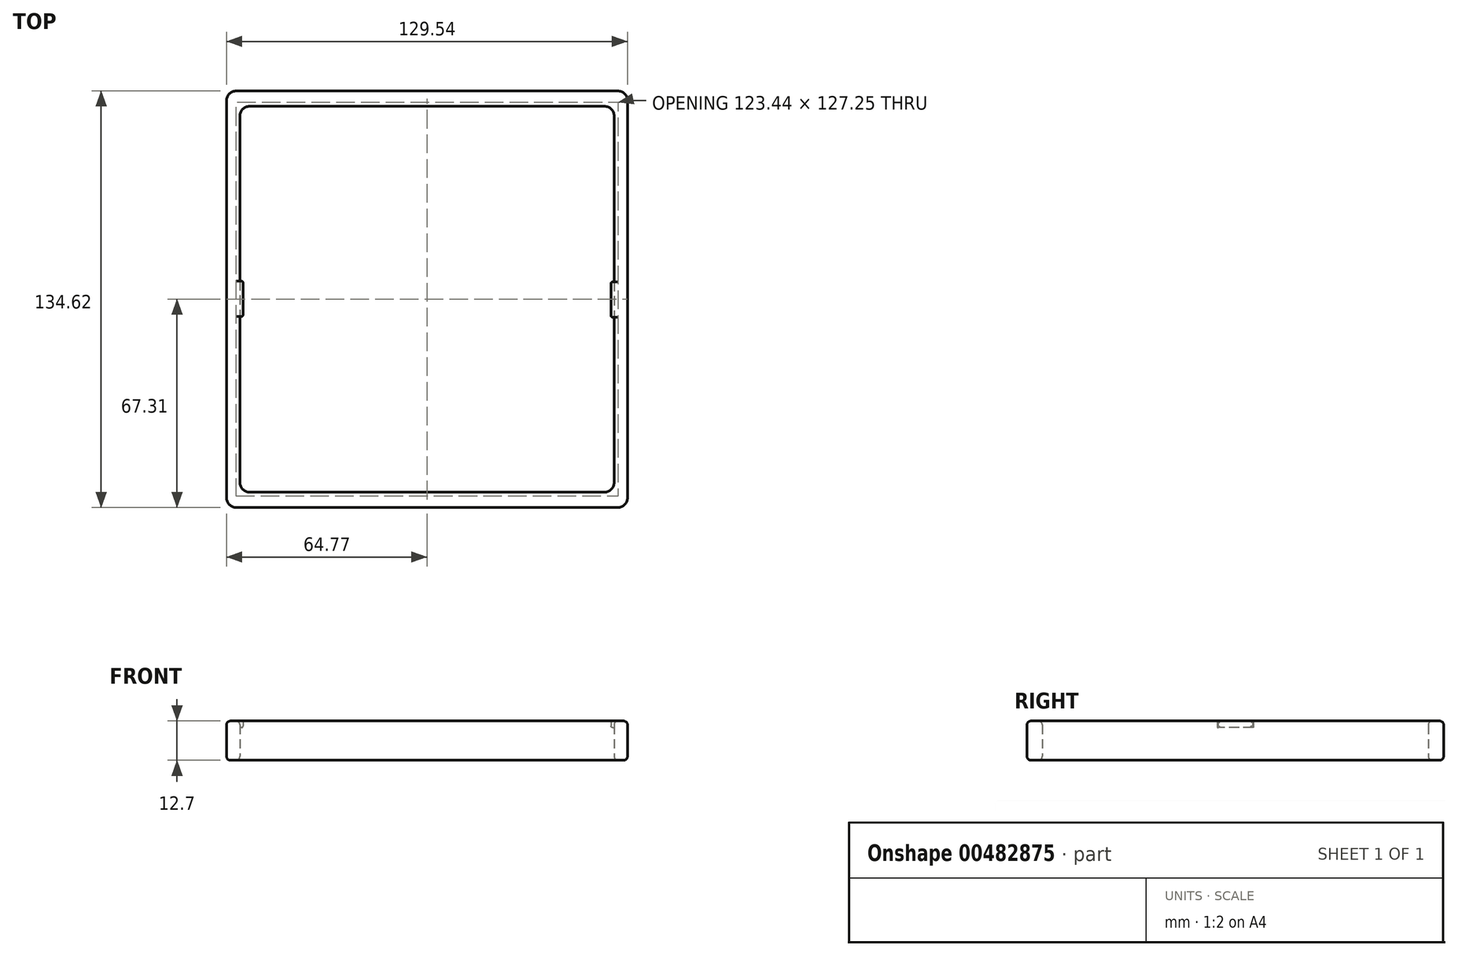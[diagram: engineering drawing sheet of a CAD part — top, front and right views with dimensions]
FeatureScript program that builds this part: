
annotation { "Feature Type Name" : "Feature", "Feature Type Description" : "" }
export const myFeature = defineFeature(function(context is Context, id is Id, definition is map)
    precondition{}
    {
        {
            var Q0;
            Q0=qCreatedBy(makeId("Top.planeOp"),FACE);
            var sketch = newSketch(context, id + "F0", { "sketchPlane" : qUnion([Q0])});
            skLineSegment(sketch, "E0.bottom", {"start": v(-64.77, 67.31) * mm, "end": v(64.77, 67.31) * mm});
            skLineSegment(sketch, "E0.top", {"start": v(-64.77, -67.31) * mm, "end": v(64.77, -67.31) * mm});
            skLineSegment(sketch, "E0.left", {"start": v(-64.77, 67.31) * mm, "end": v(-64.77, -67.31) * mm});
            skLineSegment(sketch, "E0.right", {"start": v(64.77, 67.31) * mm, "end": v(64.77, -67.31) * mm});
            skPoint(sketch, "E0.middle", {"position": v(0, 0) * mm});
            skLineSegment(sketch, "E1.bottom", {"start": v(-60.45, 62.36) * mm, "end": v(60.45, 62.36) * mm});
            skLineSegment(sketch, "E1.top", {"start": v(-60.45, -62.36) * mm, "end": v(60.45, -62.36) * mm});
            skLineSegment(sketch, "E1.left", {"start": v(-60.45, 62.36) * mm, "end": v(-60.45, -62.36) * mm});
            skLineSegment(sketch, "E1.right", {"start": v(60.45, 62.36) * mm, "end": v(60.45, -62.36) * mm});
            skSolve(sketch);
        }
        {
            var Q0;
            Q0=makeQuery(id+"F0.imprint","IMPRINT",FACE,{"disambiguationData":[TD([[makeQuery(id+"F0.imprint","IMPRINT",EDGE,{"derivedFrom":sQuery(id+"F0.wireOp",EDGE,"E0.bottom")}),-1.0]])]});
            extrude(context, id + "F1", {"entities" : qUnion([Q0]), "depth" : 12.7 * mm});
        }
        {
            var Q0;
            Q0=makeQuery(id+"F1.opExtrude","SWEPT_EDGE",EDGE,{"disambiguationData":[OSD([sQuery(id+"F0.wireOp",EDGE,"E1.bottom"),sQuery(id+"F0.wireOp",EDGE,"E1.left")])]});
            var Q1;
            Q1=makeQuery(id+"F1.opExtrude","SWEPT_EDGE",EDGE,{"disambiguationData":[OSD([sQuery(id+"F0.wireOp",EDGE,"E1.top"),sQuery(id+"F0.wireOp",EDGE,"E1.left")])]});
            var Q2;
            Q2=makeQuery(id+"F1.opExtrude","SWEPT_EDGE",EDGE,{"disambiguationData":[OSD([sQuery(id+"F0.wireOp",EDGE,"E1.bottom"),sQuery(id+"F0.wireOp",EDGE,"E1.right")])]});
            var Q3;
            Q3=makeQuery(id+"F1.opExtrude","SWEPT_EDGE",EDGE,{"disambiguationData":[OSD([sQuery(id+"F0.wireOp",EDGE,"E1.top"),sQuery(id+"F0.wireOp",EDGE,"E1.right")])]});
            var Q4;
            Q4=makeQuery(id+"F1.opExtrude","SWEPT_EDGE",EDGE,{"disambiguationData":[OSD([sQuery(id+"F0.wireOp",EDGE,"E0.bottom"),sQuery(id+"F0.wireOp",EDGE,"E0.left")])]});
            var Q5;
            Q5=makeQuery(id+"F1.opExtrude","SWEPT_EDGE",EDGE,{"disambiguationData":[OSD([sQuery(id+"F0.wireOp",EDGE,"E0.bottom"),sQuery(id+"F0.wireOp",EDGE,"E0.right")])]});
            var Q6;
            Q6=makeQuery(id+"F1.opExtrude","SWEPT_EDGE",EDGE,{"disambiguationData":[OSD([sQuery(id+"F0.wireOp",EDGE,"E0.top"),sQuery(id+"F0.wireOp",EDGE,"E0.left")])]});
            var Q7;
            Q7=makeQuery(id+"F1.opExtrude","SWEPT_EDGE",EDGE,{"disambiguationData":[OSD([sQuery(id+"F0.wireOp",EDGE,"E0.top"),sQuery(id+"F0.wireOp",EDGE,"E0.right")])]});
            fillet(context, id + "F2", {"entities" : qUnion([Q0, Q1, Q2, Q3, Q4, Q5, Q6, Q7]), "radius" : 3.17 * mm, "tangentPropagation" : true, "allowEdgeOverflow" : false});
        }
        {
            var Q0;
            Q0=makeQuery(id+"F1.opExtrude","SWEPT_FACE",FACE,{"disambiguationData":[OSD([sQuery(id+"F0.wireOp",EDGE,"E1.left")])]});
            var sketch = newSketch(context, id + "F3", { "sketchPlane" : qUnion([Q0])});
            skLineSegment(sketch, "E2.bottom", {"start": v(5.84, 12.7) * mm, "end": v(-5.59, 12.7) * mm});
            skLineSegment(sketch, "E2.top", {"start": v(5.84, 10.54) * mm, "end": v(-5.59, 10.54) * mm});
            skLineSegment(sketch, "E2.left", {"start": v(5.84, 12.7) * mm, "end": v(5.84, 10.54) * mm});
            skLineSegment(sketch, "E2.right", {"start": v(-5.59, 12.7) * mm, "end": v(-5.59, 10.54) * mm});
            skSolve(sketch);
        }
        {
            var Q0;
            Q0=makeQuery(id+"F1.opExtrude","SWEPT_FACE",FACE,{"disambiguationData":[OSD([sQuery(id+"F0.wireOp",EDGE,"E1.right")])]});
            var sketch = newSketch(context, id + "F4", { "sketchPlane" : qUnion([Q0])});
            skLineSegment(sketch, "E3.bottom", {"start": v(-5.59, 12.7) * mm, "end": v(5.84, 12.7) * mm});
            skLineSegment(sketch, "E3.top", {"start": v(-5.59, 10.54) * mm, "end": v(5.84, 10.54) * mm});
            skLineSegment(sketch, "E3.left", {"start": v(-5.59, 12.7) * mm, "end": v(-5.59, 10.54) * mm});
            skLineSegment(sketch, "E3.right", {"start": v(5.84, 12.7) * mm, "end": v(5.84, 10.54) * mm});
            skSolve(sketch);
        }
        {
            var Q0;
            Q0=makeQuery(id+"F4.imprint","IMPRINT",FACE,{"disambiguationData":[TD([[makeQuery(id+"F4.imprint","IMPRINT",EDGE,{"derivedFrom":sQuery(id+"F4.wireOp",EDGE,"E3.bottom")}),-1.0]])]});
            extrude(context, id + "F5", {"entities" : qUnion([Q0]), "operationType" : NewBodyOperationType.ADD, "depth" : 1.02 * mm});
        }
        {
            var Q0;
            Q0=makeQuery(id+"F3.imprint","IMPRINT",FACE,{"disambiguationData":[TD([[makeQuery(id+"F3.imprint","IMPRINT",EDGE,{"derivedFrom":sQuery(id+"F3.wireOp",EDGE,"E2.bottom")}),1.0]])]});
            extrude(context, id + "F6", {"entities" : qUnion([Q0]), "operationType" : NewBodyOperationType.ADD, "depth" : 1.02 * mm});
        }
        {
            var Q0;
            Q0=makeQuery(id+"F1.opExtrude","CAP_EDGE",EDGE,{"disambiguationData":[OSD([sQuery(id+"F0.wireOp",EDGE,"E1.top")])],"isStart":false});
            var Q1;
            Q1=makeQuery(id+"F1.opExtrude","CAP_EDGE",EDGE,{"disambiguationData":[OSD([sQuery(id+"F0.wireOp",EDGE,"E1.bottom")])],"isStart":true});
            var Q2;
            Q2=makeQuery(id+"F1.opExtrude","CAP_EDGE",EDGE,{"disambiguationData":[OSD([sQuery(id+"F0.wireOp",EDGE,"E0.left")])],"isStart":true});
            var Q3;
            {var subQ0=sQuery(id+"F0.wireOp",EDGE,"E1.left");Q3=makeQuery(id+"F6.boolean.opBoolean","SPLIT",EDGE,{"disambiguationData":[TD([makeQuery(id+"F6.opExtrude","SWEPT_FACE",FACE,{"disambiguationData":[OSD([sQuery(id+"F3.wireOp",EDGE,"E2.left")])]})])],"derivedFrom":makeQuery(id+"F1.opExtrude","CAP_EDGE",EDGE,{"disambiguationData":[OSD([subQ0])],"isStart":false})});}
            fillet(context, id + "F7", {"entities" : qUnion([Q0, Q1, Q2, Q3]), "radius" : 1.27 * mm, "tangentPropagation" : true, "allowEdgeOverflow" : false});
        }
        {
            var Q0;
            Q0=makeQuery(id+"F6.opExtrude","CAP_EDGE",EDGE,{"disambiguationData":[OSD([sQuery(id+"F3.wireOp",EDGE,"E2.left")])],"isStart":false});
            var Q1;
            Q1=makeQuery(id+"F6.opExtrude","CAP_EDGE",EDGE,{"disambiguationData":[OSD([sQuery(id+"F3.wireOp",EDGE,"E2.right")])],"isStart":false});
            var Q2;
            Q2=makeQuery(id+"F6.opExtrude","CAP_EDGE",EDGE,{"disambiguationData":[OSD([sQuery(id+"F3.wireOp",EDGE,"E2.top")])],"isStart":false});
            var Q3;
            Q3=makeQuery(id+"F6.opExtrude","CAP_EDGE",EDGE,{"disambiguationData":[OSD([sQuery(id+"F3.wireOp",EDGE,"E2.bottom")])],"isStart":false});
            var Q4;
            Q4=makeQuery(id+"F5.opExtrude","CAP_EDGE",EDGE,{"disambiguationData":[OSD([sQuery(id+"F4.wireOp",EDGE,"E3.left")])],"isStart":false});
            var Q5;
            Q5=makeQuery(id+"F5.opExtrude","CAP_EDGE",EDGE,{"disambiguationData":[OSD([sQuery(id+"F4.wireOp",EDGE,"E3.right")])],"isStart":false});
            var Q6;
            Q6=makeQuery(id+"F5.opExtrude","CAP_EDGE",EDGE,{"disambiguationData":[OSD([sQuery(id+"F4.wireOp",EDGE,"E3.bottom")])],"isStart":false});
            var Q7;
            Q7=makeQuery(id+"F5.opExtrude","CAP_EDGE",EDGE,{"disambiguationData":[OSD([sQuery(id+"F4.wireOp",EDGE,"E3.top")])],"isStart":false});
            fillet(context, id + "F8", {"entities" : qUnion([Q0, Q1, Q2, Q3, Q4, Q5, Q6, Q7]), "radius" : 0.5 * mm, "tangentPropagation" : true, "allowEdgeOverflow" : false});
        }
        {
            var Q0;
            Q0=makeQuery(id+"F1.opExtrude","SWEPT_FACE",FACE,{"disambiguationData":[OSD([sQuery(id+"F0.wireOp",EDGE,"E0.bottom")])]});
            var sketch = newSketch(context, id + "F9", { "sketchPlane" : qUnion([Q0])});
            skSolve(sketch);
        }
        {
            var Q0;
            Q0=makeQuery(id+"FzTZss518UkpoHX_1.boolean.opBoolean","COPY",EDGE,{"derivedFrom":makeQuery(id+"FzTZss518UkpoHX_1.opExtrude","SWEPT_EDGE",EDGE,{"disambiguationData":[OSD([sQuery(id+"F0.wireOp",EDGE,"E0.bottom"),sQuery(id+"F9.wireOp",EDGE,"sUkPVCZu-FmAP-wwvN-n69S-kMqxHEbbKcBE.bottom"),sQuery(id+"F9.wireOp",EDGE,"sUkPVCZu-FmAP-wwvN-n69S-kMqxHEbbKcBE.right")])]})});
            var Q1;
            Q1=makeQuery(id+"FzTZss518UkpoHX_1.boolean.opBoolean","COPY",EDGE,{"derivedFrom":makeQuery(id+"FzTZss518UkpoHX_1.opExtrude","SWEPT_EDGE",EDGE,{"disambiguationData":[OSD([sQuery(id+"F9.wireOp",EDGE,"sUkPVCZu-FmAP-wwvN-n69S-kMqxHEbbKcBE.top"),sQuery(id+"F9.wireOp",EDGE,"sUkPVCZu-FmAP-wwvN-n69S-kMqxHEbbKcBE.right")])]})});
            var Q2;
            Q2=makeQuery(id+"FzTZss518UkpoHX_1.boolean.opBoolean","COPY",EDGE,{"derivedFrom":makeQuery(id+"FzTZss518UkpoHX_1.opExtrude","SWEPT_EDGE",EDGE,{"disambiguationData":[OSD([sQuery(id+"F9.wireOp",EDGE,"sUkPVCZu-FmAP-wwvN-n69S-kMqxHEbbKcBE.top"),sQuery(id+"F9.wireOp",EDGE,"sUkPVCZu-FmAP-wwvN-n69S-kMqxHEbbKcBE.left")])]})});
            var Q3;
            Q3=makeQuery(id+"F1.opExtrude","CAP_EDGE",EDGE,{"disambiguationData":[OSD([sQuery(id+"F0.wireOp",EDGE,"E0.bottom")])],"isStart":false});
            fillet(context, id + "F10", {"entities" : qUnion([Q0, Q1, Q2, Q3]), "radius" : 1.27 * mm, "tangentPropagation" : true, "allowEdgeOverflow" : false});
        }
    });
